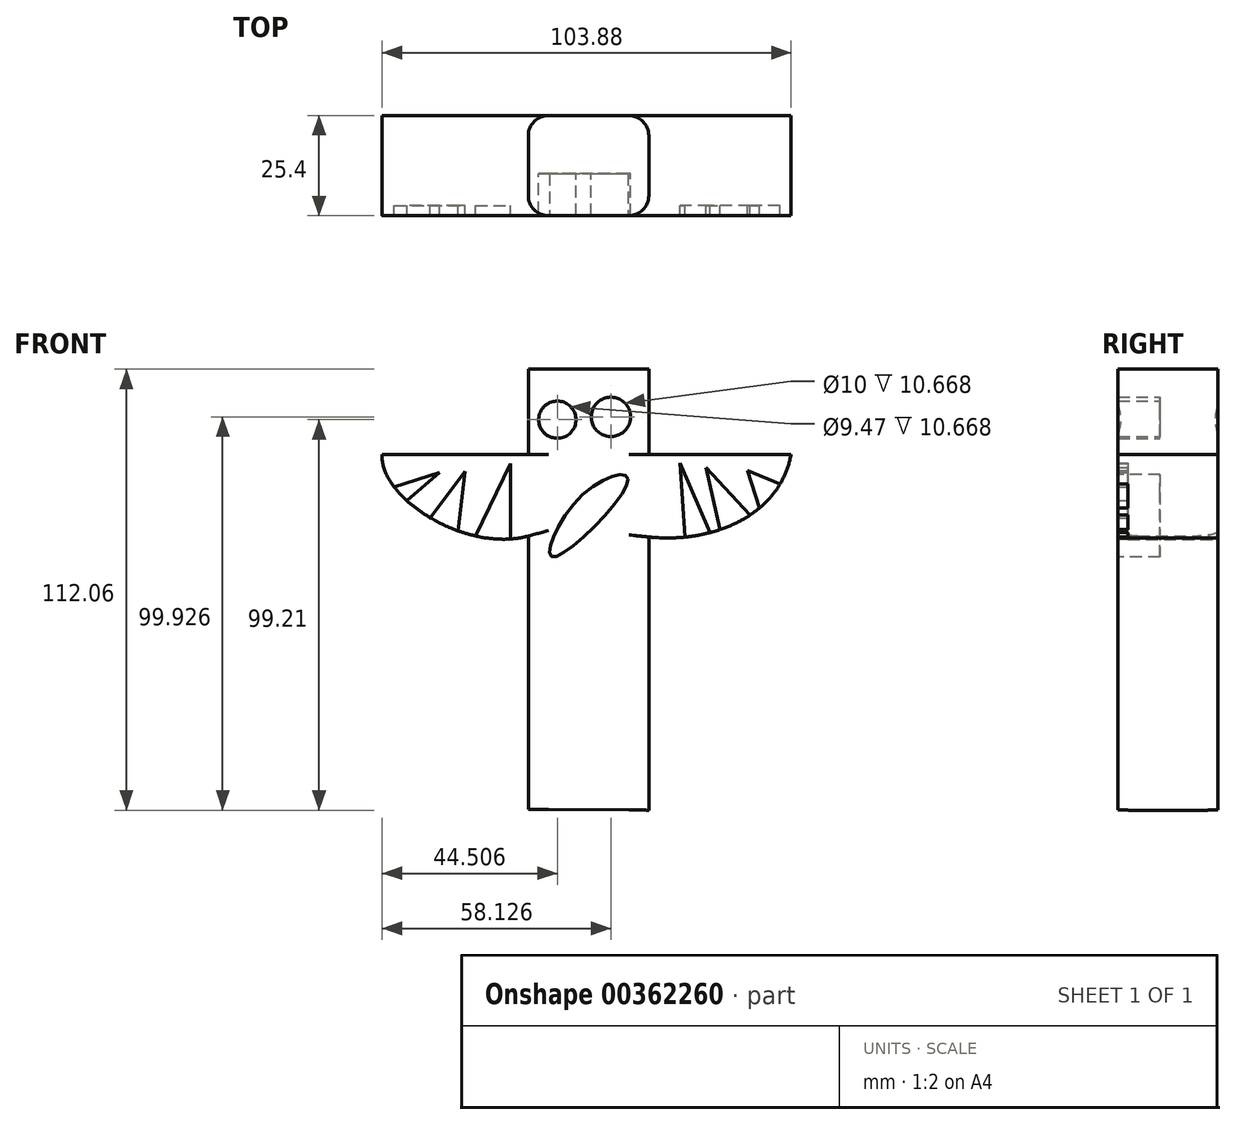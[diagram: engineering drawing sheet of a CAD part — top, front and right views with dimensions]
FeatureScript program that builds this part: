
annotation { "Feature Type Name" : "Feature", "Feature Type Description" : "" }
export const myFeature = defineFeature(function(context is Context, id is Id, definition is map)
    precondition{}
    {
        {
            var Q0;
            Q0=qCreatedBy(makeId("Front.planeOp"),FACE);
            var sketch = newSketch(context, id + "F0", { "sketchPlane" : qUnion([Q0])});
            skLineSegment(sketch, "E0", {"start": v(-15.18, -55.91) * mm, "end": v(-15.18, 55.91) * mm});
            skLineSegment(sketch, "E1", {"start": v(-15.18, 55.91) * mm, "end": v(15.42, 55.91) * mm});
            skLineSegment(sketch, "E2", {"start": v(15.42, 55.91) * mm, "end": v(15.42, -56.15) * mm});
            skLineSegment(sketch, "E3", {"start": v(15.42, -56.15) * mm, "end": v(-15.18, -55.91) * mm});
            skLineSegment(sketch, "E4", {"start": v(15.42, 34.22) * mm, "end": v(51.57, 34.22) * mm});
            skLineSegment(sketch, "E5", {"start": v(-15.18, 34.22) * mm, "end": v(-52.3, 34.22) * mm});
            skFitSpline(sketch, "E6", {"points": [v(-52.3, 34.22) * mm, v(-15.18, 13.5) * mm], "startDerivative": vector(-2.17, -33.26) * mm, "endDerivative": vector(47.72, 13.01) * mm});
            skFitSpline(sketch, "E7", {"points": [v(51.57, 34.22) * mm, v(15.42, 13.25) * mm], "startDerivative": vector(-8.68, -46.27) * mm, "endDerivative": vector(-49.89, 5.06) * mm});
            skCircle(sketch, "E8", {"center": v(-7.8, 43.06) * mm, "radius": 4.73 * mm});
            skCircle(sketch, "E9", {"center": v(5.82, 43.78) * mm, "radius": 5 * mm});
            skFitSpline(sketch, "E10", {"points": [v(-1.35, 24) * mm, v(10.14, 27.73) * mm, v(-8.81, 8.23) * mm, v(-1.35, 24) * mm]});
            skLineSegment(sketch, "E11", {"start": v(-49.28, 26.01) * mm, "end": v(-37.75, 29.6) * mm});
            skLineSegment(sketch, "E12", {"start": v(-37.75, 29.6) * mm, "end": v(-46.03, 22.5) * mm});
            skLineSegment(sketch, "E13", {"start": v(-40.1, 18.14) * mm, "end": v(-31.27, 29.93) * mm});
            skLineSegment(sketch, "E14", {"start": v(-31.27, 29.93) * mm, "end": v(-32.97, 14.8) * mm});
            skLineSegment(sketch, "E15", {"start": v(-28.56, 13.51) * mm, "end": v(-19.68, 31.96) * mm});
            skLineSegment(sketch, "E16", {"start": v(-19.68, 31.96) * mm, "end": v(-19.68, 12.75) * mm});
            skLineSegment(sketch, "E17", {"start": v(48.74, 26.67) * mm, "end": v(40.49, 30.1) * mm});
            skLineSegment(sketch, "E18", {"start": v(40.49, 30.1) * mm, "end": v(43.52, 20.59) * mm});
            skLineSegment(sketch, "E19", {"start": v(41.17, 18.83) * mm, "end": v(29.92, 30.94) * mm});
            skLineSegment(sketch, "E20", {"start": v(29.92, 30.94) * mm, "end": v(33.54, 15.13) * mm});
            skLineSegment(sketch, "E21", {"start": v(30.94, 14.35) * mm, "end": v(23.38, 32.02) * mm});
            skLineSegment(sketch, "E22", {"start": v(23.38, 32.02) * mm, "end": v(24.57, 13.23) * mm});
            skSolve(sketch);
        }
        {
            var Q0;
            {var subQ0=sQuery(id+"F0.wireOp",EDGE,"E1");Q0=makeQuery(id+"F0.imprint","IMPRINT",FACE,{"disambiguationData":[TD([[makeQuery(id+"F0.imprint","IMPRINT",EDGE,{"derivedFrom":subQ0}),-1.0]])]});}
            var Q1;
            {var subQ0=sQuery(id+"F0.wireOp",EDGE,"E5");Q1=makeQuery(id+"F0.imprint","IMPRINT",FACE,{"disambiguationData":[TD([[makeQuery(id+"F0.imprint","IMPRINT",EDGE,{"derivedFrom":subQ0}),1.0]])]});}
            var Q2;
            {var subQ0=sQuery(id+"F0.wireOp",EDGE,"E4");Q2=makeQuery(id+"F0.imprint","IMPRINT",FACE,{"disambiguationData":[TD([[makeQuery(id+"F0.imprint","IMPRINT",EDGE,{"derivedFrom":subQ0}),-1.0]])]});}
            extrude(context, id + "F1", {"entities" : qUnion([Q0, Q1, Q2]), "depth" : 25.4 * mm});
        }
        {
            var Q0;
            {var subQ0=sQuery(id+"F0.wireOp",EDGE,"E0");Q0=makeQuery(id+"F1.opExtrude","CAP_EDGE",EDGE,{"disambiguationData":[OSD([subQ0]),TDD([makeQuery(id+"F0.imprint","IMPRINT",EDGE,{"disambiguationData":[TD([[makeQuery(id+"F0.imprint","INTERSECT",VERTEX,{"derivedFrom":[subQ0,sQuery(id+"F0.wireOp",EDGE,"E1")]}),1.0]])],"derivedFrom":subQ0})])],"isStart":false});}
            var Q1;
            {var subQ0=sQuery(id+"F0.wireOp",EDGE,"E0");Q1=makeQuery(id+"F1.opExtrude","CAP_EDGE",EDGE,{"disambiguationData":[OSD([subQ0]),TDD([makeQuery(id+"F0.imprint","IMPRINT",EDGE,{"disambiguationData":[TD([[makeQuery(id+"F0.imprint","INTERSECT",VERTEX,{"derivedFrom":[subQ0,sQuery(id+"F0.wireOp",EDGE,"E1")]}),1.0]])],"derivedFrom":subQ0})])],"isStart":true});}
            var Q2;
            {var subQ0=sQuery(id+"F0.wireOp",EDGE,"E2");Q2=makeQuery(id+"F1.opExtrude","CAP_EDGE",EDGE,{"disambiguationData":[OSD([subQ0]),TDD([makeQuery(id+"F0.imprint","IMPRINT",EDGE,{"disambiguationData":[TD([[makeQuery(id+"F0.imprint","INTERSECT",VERTEX,{"derivedFrom":[sQuery(id+"F0.wireOp",EDGE,"E1"),subQ0]}),-1.0]])],"derivedFrom":subQ0})])],"isStart":false});}
            var Q3;
            {var subQ0=sQuery(id+"F0.wireOp",EDGE,"E2");Q3=makeQuery(id+"F1.opExtrude","CAP_EDGE",EDGE,{"disambiguationData":[OSD([subQ0]),TDD([makeQuery(id+"F0.imprint","IMPRINT",EDGE,{"disambiguationData":[TD([[makeQuery(id+"F0.imprint","INTERSECT",VERTEX,{"derivedFrom":[sQuery(id+"F0.wireOp",EDGE,"E1"),subQ0]}),-1.0]])],"derivedFrom":subQ0})])],"isStart":true});}
            var Q4;
            {var subQ0=sQuery(id+"F0.wireOp",EDGE,"E2");Q4=makeQuery(id+"F1.opExtrude","CAP_EDGE",EDGE,{"disambiguationData":[OSD([subQ0]),TDD([makeQuery(id+"F0.imprint","IMPRINT",EDGE,{"disambiguationData":[TD([[makeQuery(id+"F0.imprint","INTERSECT",VERTEX,{"derivedFrom":[subQ0,sQuery(id+"F0.wireOp",EDGE,"E3")]}),1.0]])],"derivedFrom":subQ0})])],"isStart":false});}
            var Q5;
            {var subQ0=sQuery(id+"F0.wireOp",EDGE,"E2");Q5=makeQuery(id+"F1.opExtrude","CAP_EDGE",EDGE,{"disambiguationData":[OSD([subQ0]),TDD([makeQuery(id+"F0.imprint","IMPRINT",EDGE,{"disambiguationData":[TD([[makeQuery(id+"F0.imprint","INTERSECT",VERTEX,{"derivedFrom":[subQ0,sQuery(id+"F0.wireOp",EDGE,"E3")]}),1.0]])],"derivedFrom":subQ0})])],"isStart":true});}
            var Q6;
            {var subQ0=sQuery(id+"F0.wireOp",EDGE,"E0");Q6=makeQuery(id+"F1.opExtrude","CAP_EDGE",EDGE,{"disambiguationData":[OSD([subQ0]),TDD([makeQuery(id+"F0.imprint","IMPRINT",EDGE,{"disambiguationData":[TD([[makeQuery(id+"F0.imprint","INTERSECT",VERTEX,{"derivedFrom":[subQ0,sQuery(id+"F0.wireOp",EDGE,"E3")]}),-1.0]])],"derivedFrom":subQ0})])],"isStart":true});}
            var Q7;
            {var subQ0=sQuery(id+"F0.wireOp",EDGE,"E0");Q7=makeQuery(id+"F1.opExtrude","CAP_EDGE",EDGE,{"disambiguationData":[OSD([subQ0]),TDD([makeQuery(id+"F0.imprint","IMPRINT",EDGE,{"disambiguationData":[TD([[makeQuery(id+"F0.imprint","INTERSECT",VERTEX,{"derivedFrom":[subQ0,sQuery(id+"F0.wireOp",EDGE,"E3")]}),-1.0]])],"derivedFrom":subQ0})])],"isStart":false});}
            fillet(context, id + "F2", {"entities" : qUnion([Q0, Q1, Q2, Q3, Q4, Q5, Q6, Q7]), "radius" : 5.08 * mm, "tangentPropagation" : true, "allowEdgeOverflow" : false});
        }
        {
            var Q0;
            Q0=makeQuery(id+"F0.imprint","IMPRINT",FACE,{"disambiguationData":[TD([[makeQuery(id+"F0.imprint","IMPRINT",EDGE,{"derivedFrom":sQuery(id+"F0.wireOp",EDGE,"E10")}),-1.0]])]});
            var Q1;
            Q1=makeQuery(id+"F0.imprint","IMPRINT",FACE,{"disambiguationData":[TD([[makeQuery(id+"F0.imprint","IMPRINT",EDGE,{"derivedFrom":sQuery(id+"F0.wireOp",EDGE,"E8")}),1.0]])]});
            var Q2;
            Q2=makeQuery(id+"F0.imprint","IMPRINT",FACE,{"disambiguationData":[TD([[makeQuery(id+"F0.imprint","IMPRINT",EDGE,{"derivedFrom":sQuery(id+"F0.wireOp",EDGE,"E9")}),1.0]])]});
            extrude(context, id + "F3", {"entities" : qUnion([Q0, Q1, Q2]), "operationType" : NewBodyOperationType.ADD, "depth" : 14.73 * mm});
        }
        {
            var Q0;
            {var subQ0=sQuery(id+"F0.wireOp",EDGE,"E11");Q0=makeQuery(id+"F0.imprint","IMPRINT",FACE,{"disambiguationData":[TD([[makeQuery(id+"F0.imprint","IMPRINT",EDGE,{"derivedFrom":subQ0}),-1.0]])]});}
            var Q1;
            {var subQ0=sQuery(id+"F0.wireOp",EDGE,"E13");Q1=makeQuery(id+"F0.imprint","IMPRINT",FACE,{"disambiguationData":[TD([[makeQuery(id+"F0.imprint","IMPRINT",EDGE,{"derivedFrom":subQ0}),-1.0]])]});}
            var Q2;
            {var subQ0=sQuery(id+"F0.wireOp",EDGE,"E15");Q2=makeQuery(id+"F0.imprint","IMPRINT",FACE,{"disambiguationData":[TD([[makeQuery(id+"F0.imprint","IMPRINT",EDGE,{"derivedFrom":subQ0}),-1.0]])]});}
            var Q3;
            {var subQ0=sQuery(id+"F0.wireOp",EDGE,"E21");Q3=makeQuery(id+"F0.imprint","IMPRINT",FACE,{"disambiguationData":[TD([[makeQuery(id+"F0.imprint","IMPRINT",EDGE,{"derivedFrom":subQ0}),1.0]])]});}
            var Q4;
            {var subQ0=sQuery(id+"F0.wireOp",EDGE,"E19");Q4=makeQuery(id+"F0.imprint","IMPRINT",FACE,{"disambiguationData":[TD([[makeQuery(id+"F0.imprint","IMPRINT",EDGE,{"derivedFrom":subQ0}),1.0]])]});}
            var Q5;
            {var subQ0=sQuery(id+"F0.wireOp",EDGE,"E17");Q5=makeQuery(id+"F0.imprint","IMPRINT",FACE,{"disambiguationData":[TD([[makeQuery(id+"F0.imprint","IMPRINT",EDGE,{"derivedFrom":subQ0}),1.0]])]});}
            extrude(context, id + "F4", {"entities" : qUnion([Q0, Q1, Q2, Q3, Q4, Q5]), "operationType" : NewBodyOperationType.ADD, "depth" : 22.86 * mm});
        }
    });
